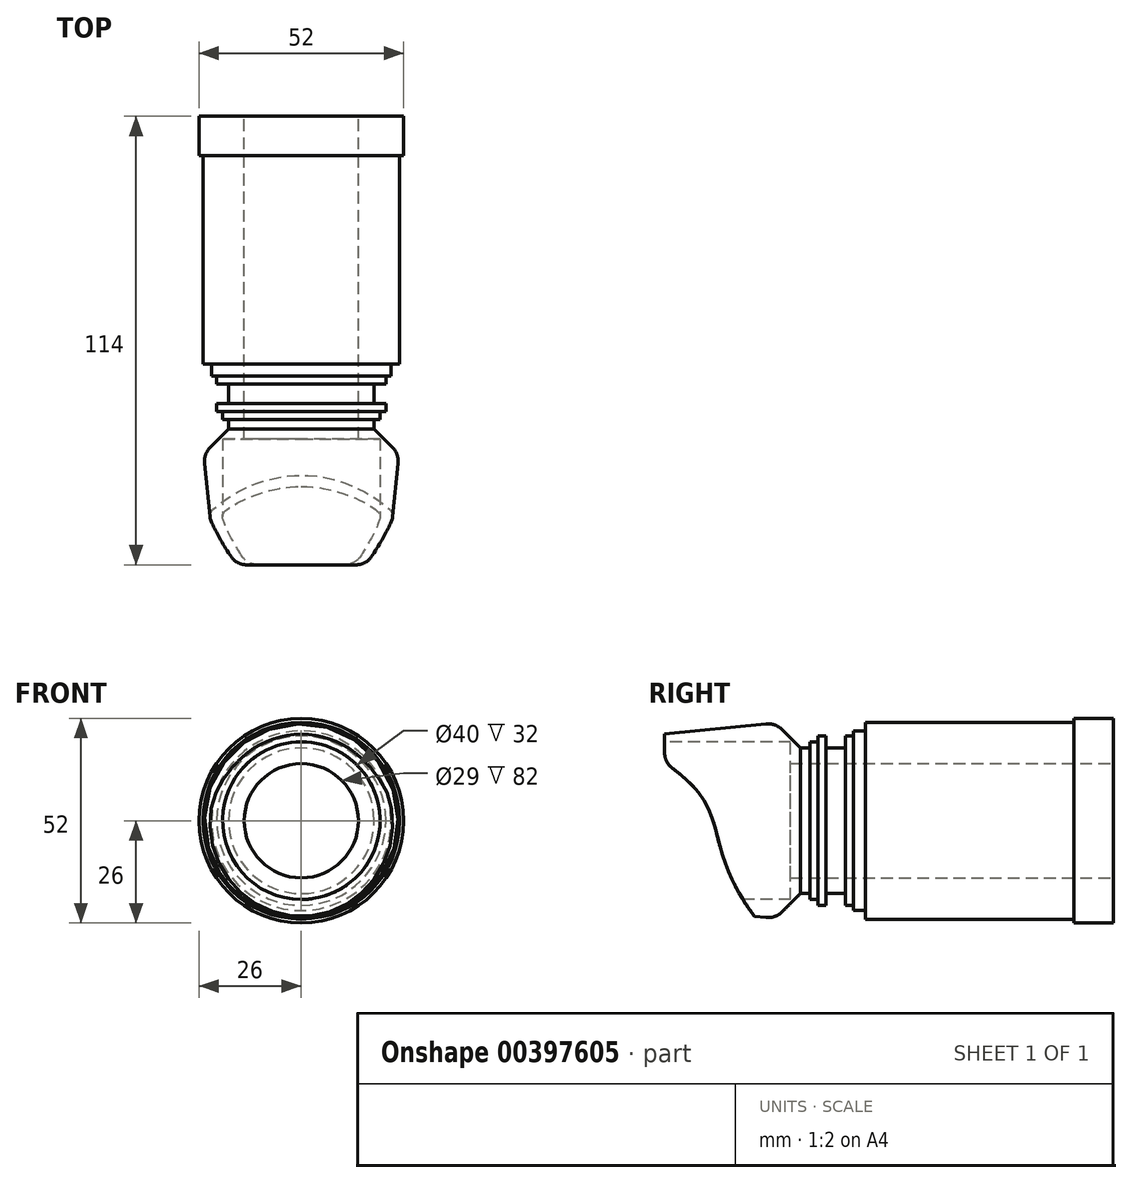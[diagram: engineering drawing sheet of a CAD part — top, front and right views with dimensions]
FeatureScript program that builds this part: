
annotation { "Feature Type Name" : "Feature", "Feature Type Description" : "" }
export const myFeature = defineFeature(function(context is Context, id is Id, definition is map)
    precondition{}
    {
        {
            var Q0;
            Q0=qCreatedBy(makeId("Front.planeOp"),FACE);
            var sketch = newSketch(context, id + "F0", { "sketchPlane" : qUnion([Q0])});
            skCircle(sketch, "E0", {"center": v(0, 0) * mm, "radius": 25 * mm});
            skSolve(sketch);
        }
        {
            var Q0;
            Q0=qSketchRegion(id+"F0",true);
            extrude(context, id + "F1", {"entities" : qUnion([Q0]), "depth" : 53 * mm});
        }
        {
            var Q0;
            Q0=makeQuery(id+"F1.opExtrude","CAP_FACE",FACE,{"disambiguationData":[OSD([sQuery(id+"F0.wireOp",EDGE,"E0")])],"isStart":true});
            var sketch = newSketch(context, id + "F2", { "sketchPlane" : qUnion([Q0])});
            skCircle(sketch, "E1", {"center": v(0, 0) * mm, "radius": 26 * mm});
            skSolve(sketch);
        }
        {
            var Q0;
            Q0=qSketchRegion(id+"F2",true);
            extrude(context, id + "F3", {"entities" : qUnion([Q0]), "operationType" : NewBodyOperationType.ADD, "depth" : 10 * mm});
        }
        {
            var Q0;
            Q0=makeQuery(id+"F1.opExtrude","CAP_FACE",FACE,{"disambiguationData":[OSD([sQuery(id+"F0.wireOp",EDGE,"E0")])],"isStart":false});
            var sketch = newSketch(context, id + "F4", { "sketchPlane" : qUnion([Q0])});
            skCircle(sketch, "E2", {"center": v(0, 0) * mm, "radius": 22.83 * mm});
            skSolve(sketch);
        }
        {
            var Q0;
            Q0=qSketchRegion(id+"F4",true);
            extrude(context, id + "F5", {"entities" : qUnion([Q0]), "operationType" : NewBodyOperationType.ADD, "depth" : 3 * mm});
        }
        {
            var Q0;
            Q0=makeQuery(id+"F5.opExtrude","CAP_FACE",FACE,{"disambiguationData":[OSD([sQuery(id+"F4.wireOp",EDGE,"E2")])],"isStart":false});
            var sketch = newSketch(context, id + "F6", { "sketchPlane" : qUnion([Q0])});
            skCircle(sketch, "E3", {"center": v(0, 0) * mm, "radius": 21.5 * mm});
            skSolve(sketch);
        }
        {
            var Q0;
            Q0=makeQuery(id+"F6.imprint","IMPRINT",FACE,{"disambiguationData":[TD([[makeQuery(id+"F6.imprint","IMPRINT",EDGE,{"derivedFrom":sQuery(id+"F6.wireOp",EDGE,"E3")}),1.0]])]});
            extrude(context, id + "F7", {"entities" : qUnion([Q0]), "operationType" : NewBodyOperationType.ADD, "depth" : 2 * mm});
        }
        {
            var Q0;
            Q0=makeQuery(id+"F7.opExtrude","CAP_FACE",FACE,{"disambiguationData":[OSD([sQuery(id+"F6.wireOp",EDGE,"E3")])],"isStart":false});
            var sketch = newSketch(context, id + "F8", { "sketchPlane" : qUnion([Q0])});
            skCircle(sketch, "E4", {"center": v(0, 0) * mm, "radius": 18.5 * mm});
            skSolve(sketch);
        }
        {
            var Q0;
            Q0=makeQuery(id+"F8.imprint","IMPRINT",FACE,{"disambiguationData":[TD([[makeQuery(id+"F8.imprint","IMPRINT",EDGE,{"derivedFrom":sQuery(id+"F8.wireOp",EDGE,"E4")}),1.0]])]});
            extrude(context, id + "F9", {"entities" : qUnion([Q0]), "operationType" : NewBodyOperationType.ADD, "depth" : 5 * mm});
        }
        {
            var Q0;
            Q0=makeQuery(id+"F9.opExtrude","CAP_FACE",FACE,{"disambiguationData":[OSD([sQuery(id+"F8.wireOp",EDGE,"E4")])],"isStart":false});
            var sketch = newSketch(context, id + "F10", { "sketchPlane" : qUnion([Q0])});
            skCircle(sketch, "E5", {"center": v(0, 0) * mm, "radius": 21.5 * mm});
            skSolve(sketch);
        }
        {
            var Q0;
            Q0=qSketchRegion(id+"F10",true);
            extrude(context, id + "F11", {"entities" : qUnion([Q0]), "operationType" : NewBodyOperationType.ADD, "depth" : 2 * mm});
        }
        {
            var Q0;
            Q0=makeQuery(id+"F11.opExtrude","CAP_FACE",FACE,{"disambiguationData":[OSD([sQuery(id+"F10.wireOp",EDGE,"E5")])],"isStart":false});
            var sketch = newSketch(context, id + "F12", { "sketchPlane" : qUnion([Q0])});
            skCircle(sketch, "E6", {"center": v(0, 0) * mm, "radius": 20 * mm});
            skSolve(sketch);
        }
        {
            var Q0;
            Q0=qSketchRegion(id+"F12",true);
            extrude(context, id + "F13", {"entities" : qUnion([Q0]), "operationType" : NewBodyOperationType.ADD, "depth" : 2 * mm});
        }
        {
            var Q0;
            Q0=makeQuery(id+"F13.opExtrude","CAP_FACE",FACE,{"disambiguationData":[OSD([sQuery(id+"F12.wireOp",EDGE,"E6")])],"isStart":false});
            var sketch = newSketch(context, id + "F14", { "sketchPlane" : qUnion([Q0])});
            skCircle(sketch, "E7", {"center": v(0, 0) * mm, "radius": 18.5 * mm});
            skSolve(sketch);
        }
        {
            var Q0;
            Q0=qSketchRegion(id+"F14",true);
            extrude(context, id + "F15", {"entities" : qUnion([Q0]), "operationType" : NewBodyOperationType.ADD, "depth" : 2 * mm});
        }
        {
            var Q0;
            Q0=makeQuery(id+"F15.opExtrude","CAP_FACE",FACE,{"disambiguationData":[OSD([sQuery(id+"F14.wireOp",EDGE,"E7")])],"isStart":false});
            var sketch = newSketch(context, id + "F16", { "sketchPlane" : qUnion([Q0])});
            skCircle(sketch, "E8", {"center": v(0, 0) * mm, "radius": 25 * mm});
            skSolve(sketch);
        }
        {
            var Q0;
            Q0=qSketchRegion(id+"F16",true);
            extrude(context, id + "F17", {"entities" : qUnion([Q0]), "operationType" : NewBodyOperationType.ADD, "depth" : 35 * mm});
        }
        {
            var Q0;
            Q0=makeQuery(id+"F17.opExtrude","CAP_FACE",FACE,{"disambiguationData":[OSD([sQuery(id+"F16.wireOp",EDGE,"E8")])],"isStart":false});
            var sketch = newSketch(context, id + "F18", { "sketchPlane" : qUnion([Q0])});
            skCircle(sketch, "E9", {"center": v(0, 0) * mm, "radius": 20 * mm});
            skSolve(sketch);
        }
        {
            var Q0;
            Q0=qSketchRegion(id+"F18",true);
            extrude(context, id + "F19", {"entities" : qUnion([Q0]), "operationType" : NewBodyOperationType.REMOVE, "oppositeDirection" : true, "depth" : 32 * mm});
        }
        {
            var Q0;
            Q0=makeQuery(id+"F17.opExtrude","CAP_EDGE",EDGE,{"disambiguationData":[OSD([sQuery(id+"F16.wireOp",EDGE,"E8")])],"isStart":true});
            chamfer(context, id + "F20", {"entities" : qUnion([Q0]), "width" : 7 * mm, "tangentPropagation" : true});
        }
        {
            var Q0;
            Q0=makeQuery(id+"F17.opExtrude","CAP_EDGE",EDGE,{"disambiguationData":[OSD([sQuery(id+"F16.wireOp",EDGE,"E8")])],"isStart":false});
            chamfer(context, id + "F21", {"entities" : qUnion([Q0]), "chamferType" : ChamferType.TWO_OFFSETS, "width1" : 3 * mm, "oppositeDirection" : false, "width2" : 30 * mm, "tangentPropagation" : true});
        }
        {
            var Q0;
            {var subQ0=sQuery(id+"F16.wireOp",EDGE,"E8");Q0=makeQuery(id+"F21.opChamfer","BLEND_EDGE",EDGE,{"blendedFrom":[makeQuery(id+"F17.opExtrude","CAP_EDGE",EDGE,{"disambiguationData":[OSD([subQ0])],"isStart":false}),makeQuery(id+"F20.opChamfer","BLEND_FACE",FACE,{"disambiguationData":[OSD([subQ0])]})],"blendedInto":[makeQuery(id+"F20.opChamfer","BLEND_FACE",FACE,{"disambiguationData":[OSD([subQ0])]})]});}
            fillet(context, id + "F22", {"entities" : qUnion([Q0]), "radius" : 5 * mm, "tangentPropagation" : true, "allowEdgeOverflow" : false});
        }
        {
            var Q0;
            Q0=qCreatedBy(makeId("Right.planeOp"),FACE);
            cPlane(context, id + "F23", {"entities" : qUnion([Q0]), "cplaneType" : CPlaneType.OFFSET, "offset" : 26.9 * mm, "width" : 150 * mm, "height" : 150 * mm});
        }
        {
            var Q0;
            Q0=qCreatedBy(id+"F23.planeOp",FACE);
            var sketch = newSketch(context, id + "F24", { "sketchPlane" : qUnion([Q0])});
            skLineSegment(sketch, "E10", {"start": v(0, 0) * mm, "end": v(-78, 0) * mm});
            skLineSegment(sketch, "E11", {"start": v(-78, 0) * mm, "end": v(-78, -31.05) * mm});
            skFitSpline(sketch, "E12", {"points": [v(-78, -28.4) * mm, v(-107.4, 17.05) * mm], "startDerivative": vector(-61.86, 75.7) * mm, "endDerivative": vector(-74.86, 47.26) * mm});
            skLineSegment(sketch, "E13", {"start": v(-78, -31.05) * mm, "end": v(-107.4, -31.05) * mm});
            skLineSegment(sketch, "E14", {"start": v(-107.4, -31.05) * mm, "end": v(-107.4, 17.05) * mm});
            skSolve(sketch);
        }
        {
            var Q0;
            {var subQ2=sQuery(id+"F24.wireOp",EDGE,"E12");Q0=makeQuery(id+"F24.imprint","IMPRINT",FACE,{"disambiguationData":[TD([[makeQuery(id+"F24.imprint","IMPRINT",EDGE,{"derivedFrom":subQ2}),1.0]])]});}
            extrude(context, id + "F25", {"entities" : qUnion([Q0]), "operationType" : NewBodyOperationType.REMOVE, "oppositeDirection" : true, "depth" : 52.3 * mm});
        }
        {
            var Q0;
            Q0=makeQuery(id+"F25.boolean.opBoolean","INTERSECT",EDGE,{"derivedFrom":[makeQuery(id+"F17.opExtrude","CAP_FACE",FACE,{"disambiguationData":[OSD([sQuery(id+"F16.wireOp",EDGE,"E8")])],"isStart":false}),makeQuery(id+"F25.opExtrude","SWEPT_FACE",FACE,{"disambiguationData":[OSD([sQuery(id+"F24.wireOp",EDGE,"E12")])]})]});
            fillet(context, id + "F26", {"entities" : qUnion([Q0]), "radius" : 5 * mm, "tangentPropagation" : true, "allowEdgeOverflow" : false});
        }
        {
            var Q0;
            Q0=makeQuery(id+"F3.opExtrude","CAP_FACE",FACE,{"disambiguationData":[OSD([sQuery(id+"F2.wireOp",EDGE,"E1")])],"isStart":false});
            var sketch = newSketch(context, id + "F27", { "sketchPlane" : qUnion([Q0])});
            skCircle(sketch, "E15", {"center": v(0, 0) * mm, "radius": 14.5 * mm});
            skSolve(sketch);
        }
        {
            var Q0;
            Q0=qSketchRegion(id+"F27",true);
            extrude(context, id + "F28", {"entities" : qUnion([Q0]), "operationType" : NewBodyOperationType.REMOVE, "oppositeDirection" : true, "depth" : 128 * mm});
        }
    });
